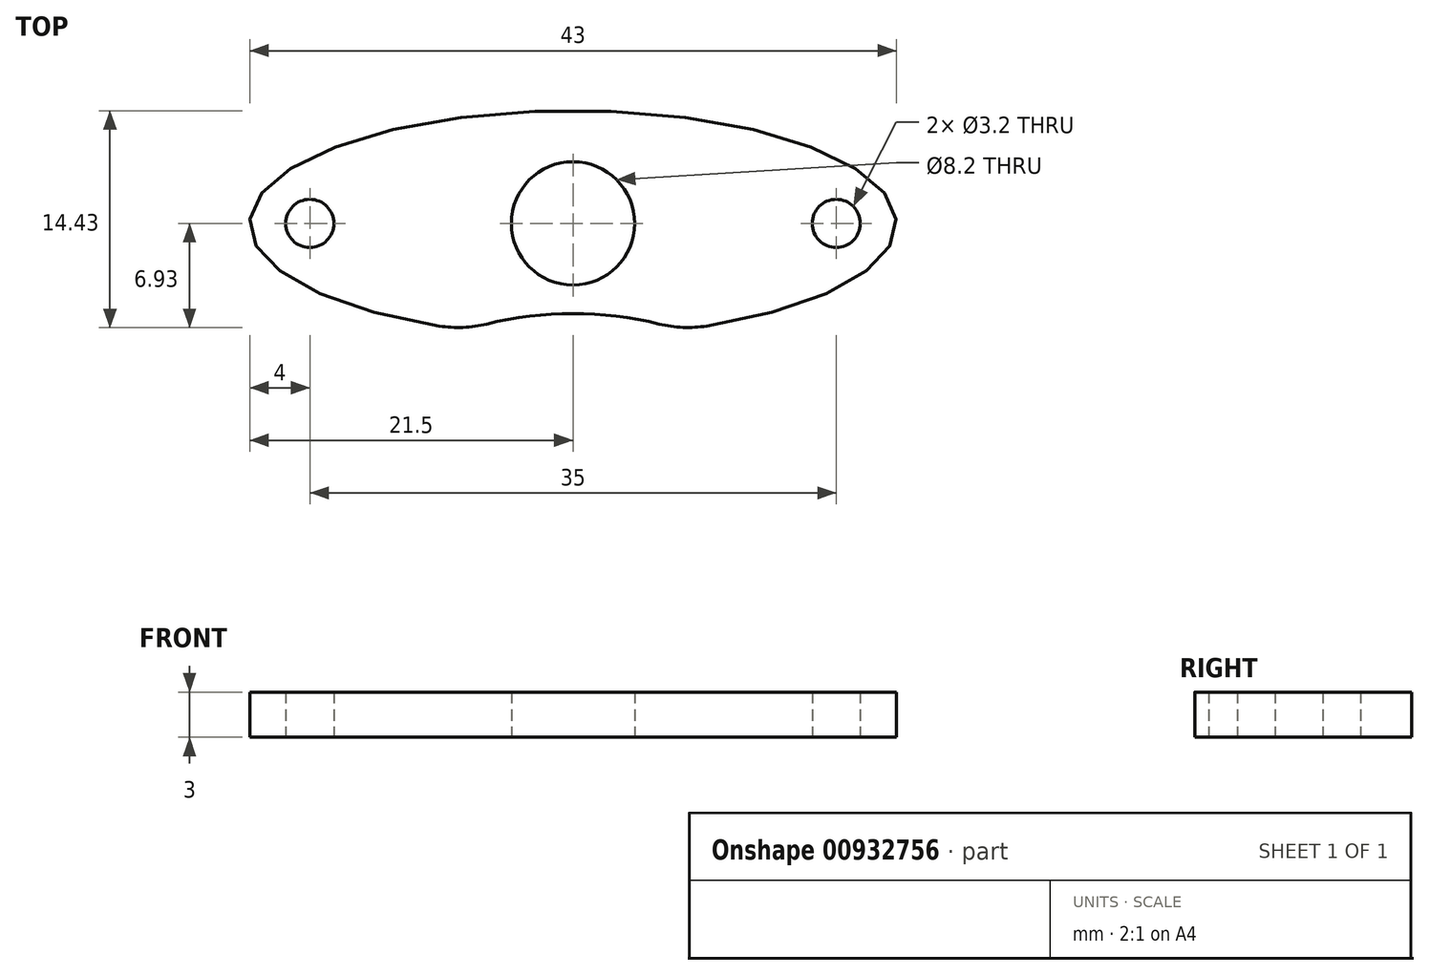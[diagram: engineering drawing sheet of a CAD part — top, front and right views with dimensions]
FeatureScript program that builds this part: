
annotation { "Feature Type Name" : "Feature", "Feature Type Description" : "" }
export const myFeature = defineFeature(function(context is Context, id is Id, definition is map)
    precondition{}
    {
        {
            var Q0;
            Q0=qCreatedBy(makeId("Top.planeOp"),FACE);
            var sketch = newSketch(context, id + "F0", { "sketchPlane" : qUnion([Q0])});
            skCircle(sketch, "E0", {"center": v(17.5, 0) * mm, "radius": 1.6 * mm});
            skArc(sketch, "E1", {"start": v(5.73, -6.7) * mm, "mid": v(0, -6) * mm, "end": v(-5.73, -6.7) * mm});
            skArc(sketch, "E2", {"start": v(5.73, -6.7) * mm, "mid": v(7.3, -6.92) * mm, "end": v(8.9, -6.83) * mm});
            skArc(sketch, "E3", {"start": v(-8.9, -6.83) * mm, "mid": v(-7.3, -6.92) * mm, "end": v(-5.73, -6.7) * mm});
            skCircle(sketch, "E4", {"center": v(-17.5, 0) * mm, "radius": 1.6 * mm});
            skEllipticalArc(sketch, "E5", {});
            skCircle(sketch, "E6", {"center": v(0, 0) * mm, "radius": 4.1 * mm});
            skLineSegment(sketch, "E7", {"start": v(-17.5, 0) * mm, "end": v(0, 0) * mm, "construction": true});
            skLineSegment(sketch, "E8", {"start": v(17.5, 0) * mm, "end": v(0, 0) * mm, "construction": true});
            skLineSegment(sketch, "E9", {"start": v(0, -30) * mm, "end": v(0, 0) * mm, "construction": true});
            skLineSegment(sketch, "E10", {"start": v(-7.64, 1.07) * mm, "end": v(7.64, 1.07) * mm, "construction": true});
            const initialGuessF0  = {"E5": [0, 0, -1, 0, 0.0215, 0.0075, 1.997437478920955, 1.1441551746688388]};
            skSetInitialGuess(sketch, initialGuessF0);
            skSolve(sketch);
        }
        {
            var Q0;
            Q0=qSketchRegion(id+"F0",true);
            extrude(context, id + "F1", {"entities" : qUnion([Q0]), "depth" : 3 * mm, "offsetDistance" : 25 * mm});
        }
    });
